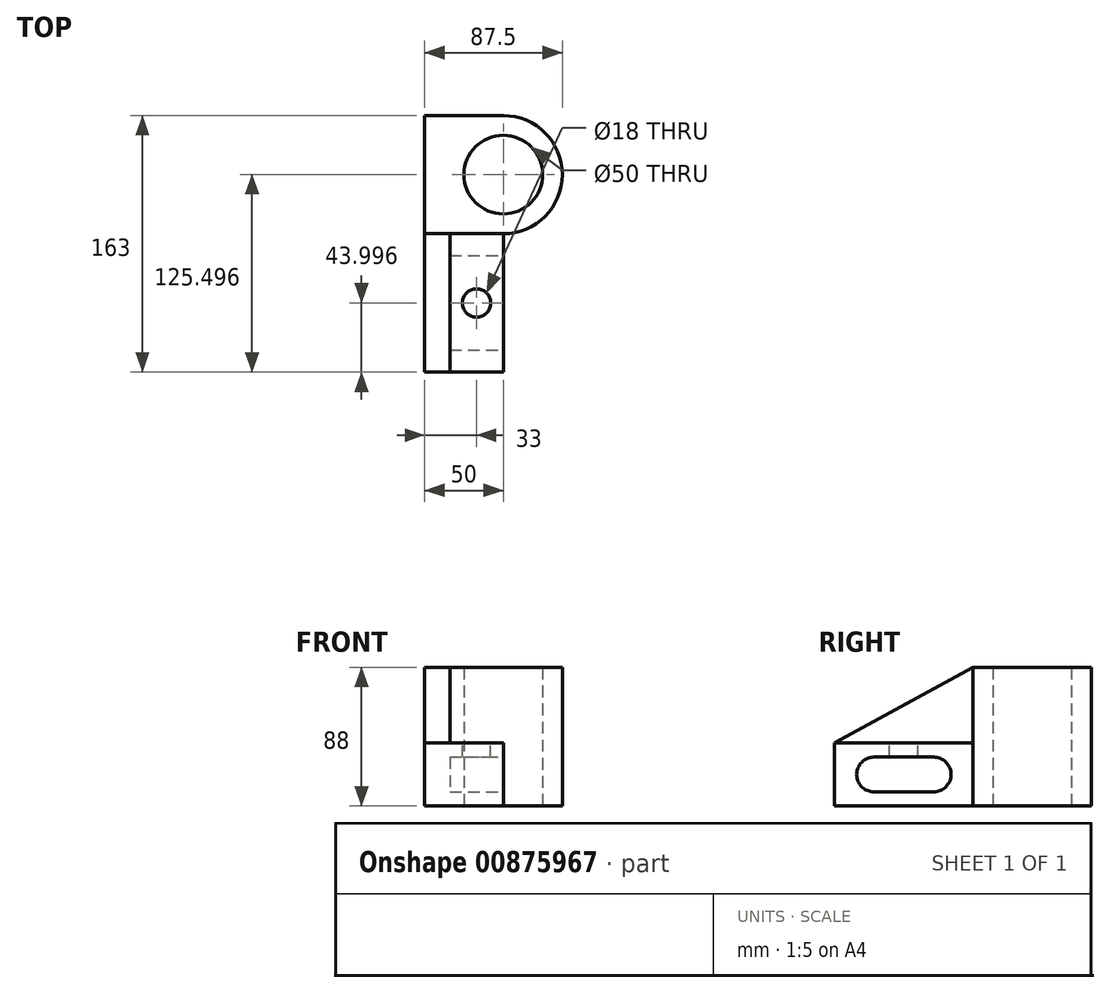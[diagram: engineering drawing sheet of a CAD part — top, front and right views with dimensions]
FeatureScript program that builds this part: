
annotation { "Feature Type Name" : "Feature", "Feature Type Description" : "" }
export const myFeature = defineFeature(function(context is Context, id is Id, definition is map)
    precondition{}
    {
        {
            var Q0;
            Q0=qCreatedBy(makeId("Top.planeOp"),FACE);
            var sketch = newSketch(context, id + "F0", { "sketchPlane" : qUnion([Q0])});
            skLineSegment(sketch, "E0.bottom", {"start": v(-50, 58.32) * mm, "end": v(0, 58.32) * mm});
            skLineSegment(sketch, "E0.top", {"start": v(-50, -16.68) * mm, "end": v(0, -16.68) * mm});
            skLineSegment(sketch, "E0.left", {"start": v(-50, 58.32) * mm, "end": v(-50, -16.68) * mm});
            skLineSegment(sketch, "E0.right", {"start": v(0, 58.32) * mm, "end": v(0, -16.68) * mm});
            skArc(sketch, "E1", {"start": v(0, -16.68) * mm, "mid": v(37.5, 20.82) * mm, "end": v(0, 58.32) * mm});
            skCircle(sketch, "E2", {"center": v(0, 20.82) * mm, "radius": 25 * mm});
            skLineSegment(sketch, "E3.top", {"start": v(-50, -104.68) * mm, "end": v(0, -104.68) * mm});
            skLineSegment(sketch, "E3.left", {"start": v(-50, -16.68) * mm, "end": v(-50, -104.68) * mm});
            skLineSegment(sketch, "E3.right", {"start": v(0, -16.68) * mm, "end": v(0, -104.68) * mm});
            skSolve(sketch);
        }
        {
            var Q0;
            Q0=makeQuery(id+"F0.imprint","IMPRINT",FACE,{"disambiguationData":[TD([[makeQuery(id+"F0.imprint","IMPRINT",EDGE,{"derivedFrom":sQuery(id+"F0.wireOp",EDGE,"E0.top")}),-1.0]])]});
            var Q1;
            {var subQ5=sQuery(id+"F0.wireOp",EDGE,"E0.bottom");Q1=makeQuery(id+"F0.imprint","IMPRINT",FACE,{"disambiguationData":[TD([[makeQuery(id+"F0.imprint","IMPRINT",EDGE,{"derivedFrom":subQ5}),-1.0]])]});}
            var Q2;
            {var subQ0=sQuery(id+"F0.wireOp",EDGE,"E1");Q2=makeQuery(id+"F0.imprint","IMPRINT",FACE,{"disambiguationData":[TD([[makeQuery(id+"F0.imprint","IMPRINT",EDGE,{"derivedFrom":subQ0}),1.0]])]});}
            extrude(context, id + "F1", {"entities" : qUnion([Q0, Q1, Q2]), "depth" : 88 * mm, "offsetDistance" : 25 * mm});
        }
        {
            var Q0;
            Q0=makeQuery(id+"F1.opExtrude","CAP_FACE",FACE,{"disambiguationData":[OSD([sQuery(id+"F0.wireOp",EDGE,"E0.bottom"),sQuery(id+"F0.wireOp",EDGE,"E0.left"),sQuery(id+"F0.wireOp",EDGE,"E1"),sQuery(id+"F0.wireOp",EDGE,"E2"),sQuery(id+"F0.wireOp",EDGE,"E3.top"),sQuery(id+"F0.wireOp",EDGE,"E3.left"),sQuery(id+"F0.wireOp",EDGE,"E3.right")])],"isStart":false});
            var sketch = newSketch(context, id + "F2", { "sketchPlane" : qUnion([Q0])});
            skLineSegment(sketch, "E4", {"start": v(0, -16.68) * mm, "end": v(-50, -16.68) * mm});
            skSolve(sketch);
        }
        {
            var Q0;
            {var subQ0=sQuery(id+"F2.wireOp",EDGE,"E4");Q0=makeQuery(id+"F2.imprint","IMPRINT",FACE,{"disambiguationData":[TD([[makeQuery(id+"F2.imprint","IMPRINT",EDGE,{"derivedFrom":subQ0}),1.0]])]});}
            extrude(context, id + "F3", {"entities" : qUnion([Q0]), "operationType" : NewBodyOperationType.REMOVE, "oppositeDirection" : true, "depth" : 48 * mm, "offsetDistance" : 25 * mm});
        }
        {
            var Q0;
            Q0=makeQuery(id+"F3.boolean.opBoolean","COPY",FACE,{"derivedFrom":makeQuery(id+"F3.opExtrude","CAP_FACE",FACE,{"disambiguationData":[OSD([sQuery(id+"F0.wireOp",EDGE,"E0.left"),sQuery(id+"F0.wireOp",EDGE,"E3.top"),sQuery(id+"F0.wireOp",EDGE,"E3.left"),sQuery(id+"F0.wireOp",EDGE,"E3.right"),sQuery(id+"F2.wireOp",EDGE,"E4")])],"isStart":false})});
            var sketch = newSketch(context, id + "F4", { "sketchPlane" : qUnion([Q0])});
            skLineSegment(sketch, "E5", {"start": v(-50, -16.68) * mm, "end": v(-34, -16.68) * mm});
            skLineSegment(sketch, "E6", {"start": v(-34, -16.68) * mm, "end": v(-34, -104.68) * mm});
            skSolve(sketch);
        }
        {
            var Q0;
            Q0=makeQuery(id+"F4.imprint","IMPRINT",FACE,{"disambiguationData":[TD([[makeQuery(id+"F4.imprint","IMPRINT",EDGE,{"derivedFrom":sQuery(id+"F4.wireOp",EDGE,"E5")}),1.0]])]});
            extrude(context, id + "F5", {"entities" : qUnion([Q0]), "operationType" : NewBodyOperationType.ADD, "depth" : 48 * mm, "offsetDistance" : 25 * mm});
        }
        {
            var Q0;
            Q0=makeQuery(id+"F5.opExtrude","SWEPT_FACE",FACE,{"disambiguationData":[OSD([sQuery(id+"F4.wireOp",EDGE,"E6")])]});
            var sketch = newSketch(context, id + "F6", { "sketchPlane" : qUnion([Q0])});
            skLineSegment(sketch, "E7", {"start": v(-104.68, 40) * mm, "end": v(-16.68, 88) * mm});
            skSolve(sketch);
        }
        {
            var Q0;
            Q0 = qSketchRegion(id + "F6", true);
            var Q1;
            Q1=makeQuery(id+"F6.imprint","IMPRINT",FACE,{"disambiguationData":[TD([[makeQuery(id+"F6.imprint","IMPRINT",EDGE,{"derivedFrom":sQuery(id+"F6.wireOp",EDGE,"E7")}),1.0]])]});
            extrude(context, id + "F7", {"entities" : qUnion([Q0, Q1]), "operationType" : NewBodyOperationType.REMOVE, "oppositeDirection" : true, "depth" : 25 * mm, "offsetDistance" : 25 * mm});
        }
        {
            var Q0;
            Q0=makeQuery(id+"F3.boolean.opBoolean","COPY",FACE,{"derivedFrom":makeQuery(id+"F3.opExtrude","CAP_FACE",FACE,{"disambiguationData":[OSD([sQuery(id+"F0.wireOp",EDGE,"E0.left"),sQuery(id+"F0.wireOp",EDGE,"E3.top"),sQuery(id+"F0.wireOp",EDGE,"E3.left"),sQuery(id+"F0.wireOp",EDGE,"E3.right"),sQuery(id+"F2.wireOp",EDGE,"E4")])],"isStart":false})});
            var sketch = newSketch(context, id + "F8", { "sketchPlane" : qUnion([Q0])});
            skCircle(sketch, "E8", {"center": v(-17, -60.68) * mm, "radius": 9 * mm});
            skSolve(sketch);
        }
        {
            var Q0;
            Q0=makeQuery(id+"F8.imprint","IMPRINT",FACE,{"disambiguationData":[TD([[makeQuery(id+"F8.imprint","IMPRINT",EDGE,{"derivedFrom":sQuery(id+"F8.wireOp",EDGE,"E8")}),1.0]])]});
            extrude(context, id + "F9", {"entities" : qUnion([Q0]), "operationType" : NewBodyOperationType.REMOVE, "oppositeDirection" : true, "depth" : 31 * mm, "offsetDistance" : 25 * mm});
        }
        {
            var Q0;
            Q0=makeQuery(id+"F1.opExtrude","SWEPT_FACE",FACE,{"disambiguationData":[OSD([sQuery(id+"F0.wireOp",EDGE,"E3.right")])]});
            var sketch = newSketch(context, id + "F10", { "sketchPlane" : qUnion([Q0])});
            skLineSegment(sketch, "E9", {"start": v(-79.68, 31) * mm, "end": v(-41.68, 31) * mm});
            skLineSegment(sketch, "E10", {"start": v(-41.68, 9) * mm, "end": v(-79.68, 9) * mm});
            skArc(sketch, "E11", {"start": v(-79.68, 31) * mm, "mid": v(-90.68, 20) * mm, "end": v(-79.68, 9) * mm});
            skArc(sketch, "E12", {"start": v(-41.68, 9) * mm, "mid": v(-30.68, 20) * mm, "end": v(-41.68, 31) * mm});
            skSolve(sketch);
        }
        {
            var Q0;
            Q0=makeQuery(id+"F10.imprint","IMPRINT",FACE,{"disambiguationData":[TD([[makeQuery(id+"F10.imprint","IMPRINT",EDGE,{"derivedFrom":sQuery(id+"F10.wireOp",EDGE,"E9")}),-1.0]])]});
            extrude(context, id + "F11", {"entities" : qUnion([Q0]), "operationType" : NewBodyOperationType.REMOVE, "oppositeDirection" : true, "depth" : 34 * mm, "offsetDistance" : 25 * mm});
        }
    });
